# Revit family: KS Husky, Typ II-13, Ø 10- 88,9
name_source: partatom
category: HLS-Bauteile
revit_build: Autodesk Revit 2017 (Build: 20190507_1515(x64)
units: mm (PartAtom-declared; Revit-internal decimal feet)

## family parameters
Arbeitsebenenbasiert = Ja
Beim Laden mit Abzugskörper schneiden = Nein
Bemaßung runder Anschluss = Durchmesser verwenden
Gemeinsam genutzt = Ja
Immer vertikal = Nein
Raumberechnungspunkt = Nein
Teiletyp = Normal

## types (22) — shared parameters
Anschluss = M8/M10
Baustoffklasse = B2
Dichte Kern = 120 kg/m³
Dämmkörper = KA/PU
Fabrikat = MEFA
Firma = MEFA Befestigungs- und Montagesysteme GmbH
H1 = 2 mm  [stored 0.00656168 ft]
HGA = 16 mm  [stored 0.0524934 ft]
Kurztext1 = Kälteschelle Husky II 13
Material = Stahl
Material Mantel = Kunststoff
Materialname = DD11
Mengeneinheit = St
Oberflaeche = galvanisch verzinkt
Rohrschellentyp = Trabant
Typ = II 13
Vorgabe-Ansicht = 1219 mm
Wasserdampfdiffusionswiderstand = 7000 µ
Wärmeleitfähigkeit = 0.029 W/mK
max. Temperaturbeständigkeit = 105 °C
mittl. Nenndruckfestigkeit Kern = 1,35 N/mm²
stat. Belastung Kern = 0,27 N/mm²

## per-type parameters (varying)
- Kälteschelle Husky, Typ II-13, M8/M10, Ø 10: A=30 mm  [stored 0.0984252 ft]; Anschlußhöhe=30 mm; Artikelnummer=6830100; B=75 mm; Breite=69 mm; D=10 mm  [stored 0.0328084 ft]; D0=35 mm  [stored 0.114829 ft]; DF1=19 mm  [stored 0.062336 ft]; DF2=19 mm  [stored 0.062336 ft]; DS=13 mm; DVS=5 mm  [stored 0.0164042 ft]; Dämmstärke=13 mm; EAN=4250928440358; Gewicht=0.06 kg; Gewicht pro Bauteil=0.06 kg; H=53 mm; H2=3 mm  [stored 0.00984252 ft]; Kurztext2=10 mm Iso 13 x 36 mm M8/M10; L=36 mm  [stored 0.11811 ft]; MB=20 mm  [stored 0.0656168 ft]; MD=1 mm  [stored 0.00328084 ft]; R=18 mm  [stored 0.0590551 ft]; RM=19 mm  [stored 0.062336 ft]; Rohraußendurchmesser Kupfer=10 mm; S=56 mm; Schalenlänge=36 mm; max. zul. Last=0.08 kN; vpe=24 St
- Kälteschelle Husky, Typ II-13, M8/M10, Ø 12: A=31 mm  [stored 0.101706 ft]; Anschlußhöhe=31 mm; Artikelnummer=6830120; B=81 mm; Breite=77 mm; D=12 mm  [stored 0.0393701 ft]; D0=39 mm  [stored 0.127953 ft]; DF1=20 mm  [stored 0.0656168 ft]; DF2=20 mm  [stored 0.0656168 ft]; DS=14 mm  [stored 0.0459318 ft]; DVS=5 mm  [stored 0.0164042 ft]; Dämmstärke=14 mm  [stored 0.0459318 ft]; EAN=4250928440365; Gewicht=0.07 kg; Gewicht pro Bauteil=0.07 kg; H=57 mm; H2=3 mm  [stored 0.00984252 ft]; Kurztext2=12 mm Iso 14 x 36 mm M8/M10; L=36 mm  [stored 0.11811 ft]; MB=20 mm  [stored 0.0656168 ft]; MD=1 mm  [stored 0.00328084 ft]; R=20 mm  [stored 0.0656168 ft]; RM=21 mm  [stored 0.0688976 ft]; Rohraußendurchmesser Kunststoff=12 mm; Rohraußendurchmesser Kupfer=12 mm; S=61 mm; Schalenlänge=36 mm; max. zul. Last=0.10 kN; vpe=24 St
- Kälteschelle Husky, Typ II-13, M8/M10, Ø 15: A=30 mm  [stored 0.0984252 ft]; Anschlußhöhe=31 mm; Artikelnummer=6830150; B=81 mm; Breite=77 mm; D=15 mm  [stored 0.0492126 ft]; D0=41 mm  [stored 0.134514 ft]; DF1=19 mm  [stored 0.062336 ft]; DF2=19 mm  [stored 0.062336 ft]; DS=13 mm; DVS=5 mm  [stored 0.0164042 ft]; Dämmstärke=13 mm; EAN=4250928440372; Gewicht=0.07 kg; Gewicht pro Bauteil=0.07 kg; H=59 mm; H2=3 mm  [stored 0.00984252 ft]; Kurztext2=15 mm Iso 13 x 36 mm M8/M10; L=36 mm  [stored 0.11811 ft]; MB=20 mm  [stored 0.0656168 ft]; MD=1 mm  [stored 0.00328084 ft]; R=21 mm  [stored 0.0688976 ft]; RM=22 mm  [stored 0.0721785 ft]; Rohraußendurchmesser Kunststoff=15 mm; Rohraußendurchmesser Kupfer=15 mm; S=62 mm; Schalenlänge=36 mm; max. zul. Last=0.13 kN; vpe=24 St
- Kälteschelle Husky, Typ II-13, M8/M10, Ø 17,2: A=30 mm  [stored 0.0984252 ft]; Anschlußhöhe=31 mm; Artikelnummer=6830180; B=81 mm; Breite=77 mm; D=18 mm  [stored 0.0590551 ft]; D0=44 mm; DF1=17 mm  [stored 0.0557743 ft]; DF2=18 mm  [stored 0.0590551 ft]; DS=13 mm; DVS=5 mm  [stored 0.0164042 ft]; Dämmstärke=13 mm; EAN=4250928440389; Gewicht=0.07 kg; Gewicht pro Bauteil=0.07 kg; H=62 mm; H2=3 mm  [stored 0.00984252 ft]; Kurztext2=17,2 mm Iso 13 x 36 mm M8/M10; L=36 mm  [stored 0.11811 ft]; MB=20 mm  [stored 0.0656168 ft]; MD=1 mm  [stored 0.00328084 ft]; R=22 mm  [stored 0.0721785 ft]; RM=23 mm; Rohraußendurchmesser Kunststoff=18 mm; Rohraußendurchmesser Kupfer=18 mm; Rohraußendurchmesser Stahl=17,2 mm; S=64 mm; Schalenlänge=36 mm; max. zul. Last=0.15 kN; vpe=24 St
- Kälteschelle Husky, Typ II-13, M8/M10, Ø 20: A=32 mm  [stored 0.104987 ft]; Anschlußhöhe=33 mm; Artikelnummer=6830200; B=92 mm; Breite=88 mm; D=20 mm  [stored 0.0656168 ft]; D0=48 mm; DF1=21 mm  [stored 0.0688976 ft]; DF2=20 mm  [stored 0.0656168 ft]; DS=14 mm  [stored 0.0459318 ft]; DVS=5 mm  [stored 0.0164042 ft]; Dämmstärke=14 mm  [stored 0.0459318 ft]; EAN=4250928440396; Gewicht=0.09 kg; Gewicht pro Bauteil=0.09 kg; H=67 mm; H2=3 mm  [stored 0.00984252 ft]; Kurztext2=20 mm Iso 14 x 36 mm M8/M10; L=36 mm  [stored 0.11811 ft]; MB=20 mm  [stored 0.0656168 ft]; MD=2 mm  [stored 0.00656168 ft]; R=24 mm  [stored 0.0787402 ft]; RM=26 mm; Rohraußendurchmesser Kunststoff=20 mm; S=71 mm; Schalenlänge=36 mm; max. zul. Last=0.17 kN; vpe=24 St
- Kälteschelle Husky, Typ II-13, M8/M10, Ø 21,3: A=31 mm  [stored 0.101706 ft]; Anschlußhöhe=32 mm; Artikelnummer=6830220; B=92 mm; Breite=88 mm; D=22 mm  [stored 0.0721785 ft]; D0=48 mm; DF1=21 mm  [stored 0.0688976 ft]; DF2=20 mm  [stored 0.0656168 ft]; DS=13 mm; DVS=5 mm  [stored 0.0164042 ft]; Dämmstärke=13 mm; EAN=4250928440402; Gewicht=0.09 kg; Gewicht pro Bauteil=0.09 kg; H=67 mm; H2=3 mm  [stored 0.00984252 ft]; Kurztext2=21,3 mm Iso 13 x 36 mm M8/M10; L=36 mm  [stored 0.11811 ft]; MB=20 mm  [stored 0.0656168 ft]; MD=2 mm  [stored 0.00656168 ft]; R=24 mm  [stored 0.0787402 ft]; RM=26 mm; Rohraußendurchmesser Kupfer=22 mm; Rohraußendurchmesser Stahl=21,3 mm; S=71 mm; Schalenlänge=36 mm; max. zul. Last=0.19 kN; vpe=24 St
- Kälteschelle Husky, Typ II-13, M8/M10, Ø 26,9: A=31 mm  [stored 0.101706 ft]; Anschlußhöhe=32 mm; Artikelnummer=6830270; B=92 mm; Breite=88 mm; D=27 mm; D0=53 mm; DF1=18 mm  [stored 0.0590551 ft]; DF2=18 mm  [stored 0.0590551 ft]; DS=13 mm; DVS=5 mm  [stored 0.0164042 ft]; Dämmstärke=13 mm; EAN=4250928440426; Gewicht=0.09 kg; Gewicht pro Bauteil=0.09 kg; H=72 mm; H2=3 mm  [stored 0.00984252 ft]; Kurztext2=26,9 mm Iso 13 x 36 mm M8/M10; L=36 mm  [stored 0.11811 ft]; MB=20 mm  [stored 0.0656168 ft]; MD=2 mm  [stored 0.00656168 ft]; R=27 mm; RM=28 mm  [stored 0.0918635 ft]; Rohraußendurchmesser Stahl=26,9 mm; S=74 mm; Schalenlänge=36 mm; max. zul. Last=0.23 kN; vpe=12 St
- Kälteschelle Husky, Typ II-13, M8/M10, Ø 28: A=30 mm  [stored 0.0984252 ft]; Anschlußhöhe=32 mm; Artikelnummer=6830280; B=92 mm; Breite=88 mm; D=28 mm  [stored 0.0918635 ft]; D0=53 mm; DF1=18 mm  [stored 0.0590551 ft]; DF2=18 mm  [stored 0.0590551 ft]; DS=13 mm; DVS=5 mm  [stored 0.0164042 ft]; Dämmstärke=13 mm; EAN=4250928440433; Gewicht=0.09 kg; Gewicht pro Bauteil=0.09 kg; H=72 mm; H2=3 mm  [stored 0.00984252 ft]; Kurztext2=28 mm Iso 13 x 36 mm M8/M10; L=36 mm  [stored 0.11811 ft]; MB=20 mm  [stored 0.0656168 ft]; MD=2 mm  [stored 0.00656168 ft]; R=27 mm; RM=28 mm  [stored 0.0918635 ft]; Rohraußendurchmesser Kupfer=28 mm; S=74 mm; Schalenlänge=36 mm; max. zul. Last=0.24 kN; vpe=12 St
- Kälteschelle Husky, Typ II-13, M8/M10, Ø 31,8: A=31 mm  [stored 0.101706 ft]; Anschlußhöhe=32 mm; Artikelnummer=6830320; B=98 mm; Breite=94 mm; D=32 mm  [stored 0.104987 ft]; D0=58 mm; DF1=19 mm  [stored 0.062336 ft]; DF2=18 mm  [stored 0.0590551 ft]; DS=13 mm; DVS=5 mm  [stored 0.0164042 ft]; Dämmstärke=13 mm; EAN=4250928440440; Gewicht=0.10 kg; Gewicht pro Bauteil=0.10 kg; H=77 mm; H2=3 mm  [stored 0.00984252 ft]; Kurztext2=31,8 mm Iso 13 x 36 mm M8/M10; L=36 mm  [stored 0.11811 ft]; MB=20 mm  [stored 0.0656168 ft]; MD=2 mm  [stored 0.00656168 ft]; R=29 mm  [stored 0.0951444 ft]; RM=31 mm  [stored 0.101706 ft]; Rohraußendurchmesser Kunststoff=32 mm; Rohraußendurchmesser Stahl=31,8 mm; S=79 mm; Schalenlänge=36 mm; max. zul. Last=0.27 kN; vpe=12 St
- Kälteschelle Husky, Typ II-13, M8/M10, Ø 33,7: A=32 mm  [stored 0.104987 ft]; Anschlußhöhe=33 mm; Artikelnummer=6830340; B=104 mm; Breite=102 mm; D=34 mm; D0=62 mm; DF1=20 mm  [stored 0.0656168 ft]; DF2=19 mm  [stored 0.062336 ft]; DS=14 mm  [stored 0.0459318 ft]; DVS=5 mm  [stored 0.0164042 ft]; Dämmstärke=14 mm  [stored 0.0459318 ft]; EAN=4250928440457; Gewicht=0.11 kg; Gewicht pro Bauteil=0.11 kg; H=81 mm; H2=3 mm  [stored 0.00984252 ft]; Kurztext2=33,7 mm Iso 14 x 36 mm M8/M10; L=36 mm  [stored 0.11811 ft]; MB=20 mm  [stored 0.0656168 ft]; MD=2 mm  [stored 0.00656168 ft]; R=31 mm  [stored 0.101706 ft]; RM=33 mm  [stored 0.108268 ft]; Rohraußendurchmesser Stahl=33,7 mm; S=84 mm; Schalenlänge=36 mm; max. zul. Last=0.29 kN; vpe=12 St
- Kälteschelle Husky, Typ II-13, M8/M10, Ø 35: A=31 mm  [stored 0.101706 ft]; Anschlußhöhe=32 mm; Artikelnummer=6830350; B=104 mm; Breite=102 mm; D=35 mm  [stored 0.114829 ft]; D0=62 mm; DF1=20 mm  [stored 0.0656168 ft]; DF2=19 mm  [stored 0.062336 ft]; DS=14 mm  [stored 0.0459318 ft]; DVS=5 mm  [stored 0.0164042 ft]; Dämmstärke=14 mm  [stored 0.0459318 ft]; EAN=4250928440464; Gewicht=0.10 kg; Gewicht pro Bauteil=0.10 kg; H=81 mm; H2=3 mm  [stored 0.00984252 ft]; Kurztext2=35 mm Iso 14 x 36 mm M8/M10; L=36 mm  [stored 0.11811 ft]; MB=20 mm  [stored 0.0656168 ft]; MD=2 mm  [stored 0.00656168 ft]; R=31 mm  [stored 0.101706 ft]; RM=33 mm  [stored 0.108268 ft]; Rohraußendurchmesser Kupfer=35 mm; S=84 mm; Schalenlänge=36 mm; max. zul. Last=0.30 kN; vpe=12 St
- Kälteschelle Husky, Typ II-13, M8/M10, Ø 40: A=32 mm  [stored 0.104987 ft]; Anschlußhöhe=33 mm; Artikelnummer=6830400; B=111 mm; Breite=109 mm; D=40 mm  [stored 0.131234 ft]; D0=68 mm; DF1=20 mm  [stored 0.0656168 ft]; DF2=20 mm  [stored 0.0656168 ft]; DS=14 mm  [stored 0.0459318 ft]; DVS=5 mm  [stored 0.0164042 ft]; Dämmstärke=14 mm  [stored 0.0459318 ft]; EAN=4250928440471; Gewicht=0.11 kg; Gewicht pro Bauteil=0.11 kg; H=87 mm; H2=3 mm  [stored 0.00984252 ft]; Kurztext2=40 mm Iso 14 x 36 mm M8/M10; L=36 mm  [stored 0.11811 ft]; MB=20 mm  [stored 0.0656168 ft]; MD=2 mm  [stored 0.00656168 ft]; R=34 mm; RM=36 mm  [stored 0.11811 ft]; Rohraußendurchmesser Kunststoff=40 mm; S=91 mm; Schalenlänge=36 mm; max. zul. Last=0.34 kN; vpe=12 St
- Kälteschelle Husky, Typ II-13, M8/M10, Ø 42,4: A=31 mm  [stored 0.101706 ft]; Anschlußhöhe=32 mm; Artikelnummer=6830420; B=111 mm; Breite=109 mm; D=42 mm  [stored 0.137795 ft]; D0=70 mm; DF1=19 mm  [stored 0.062336 ft]; DF2=19 mm  [stored 0.062336 ft]; DS=14 mm  [stored 0.0459318 ft]; DVS=5 mm  [stored 0.0164042 ft]; Dämmstärke=14 mm  [stored 0.0459318 ft]; EAN=4250928440488; Gewicht=0.11 kg; Gewicht pro Bauteil=0.11 kg; H=89 mm; H2=3 mm  [stored 0.00984252 ft]; Kurztext2=42,4 mm Iso 14 x 36 mm M8/M10; L=36 mm  [stored 0.11811 ft]; MB=20 mm  [stored 0.0656168 ft]; MD=2 mm  [stored 0.00656168 ft]; R=35 mm  [stored 0.114829 ft]; RM=37 mm; Rohraußendurchmesser Kupfer=42 mm; Rohraußendurchmesser Stahl=42,4 mm; S=92 mm; Schalenlänge=36 mm; max. zul. Last=0.36 kN; vpe=12 St
- Kälteschelle Husky, Typ II-13, M8/M10, Ø 48,3: A=32 mm  [stored 0.104987 ft]; Anschlußhöhe=33 mm; Artikelnummer=6830480; B=122 mm; Breite=121 mm; D=48 mm; D0=78 mm; DF1=21 mm  [stored 0.0688976 ft]; DF2=20 mm  [stored 0.0656168 ft]; DS=15 mm  [stored 0.0492126 ft]; DVS=5 mm  [stored 0.0164042 ft]; Dämmstärke=15 mm  [stored 0.0492126 ft]; EAN=4250928440495; Gewicht=0.14 kg; Gewicht pro Bauteil=0.14 kg; H=97 mm; H2=3 mm  [stored 0.00984252 ft]; Kurztext2=48,3 mm Iso 15 x 42 mm M8/M10; L=42 mm  [stored 0.137795 ft]; MB=25 mm  [stored 0.082021 ft]; MD=2 mm  [stored 0.00656168 ft]; R=39 mm  [stored 0.127953 ft]; RM=41 mm  [stored 0.134514 ft]; Rohraußendurchmesser Stahl=48,3 mm; S=101 mm; Schalenlänge=42 mm; max. zul. Last=0.48 kN; vpe=10 St
- Kälteschelle Husky, Typ II-13, M8/M10, Ø 50: A=32 mm  [stored 0.104987 ft]; Anschlußhöhe=33 mm; Artikelnummer=6830500; B=122 mm; Breite=121 mm; D=50 mm; D0=79 mm; DF1=20 mm  [stored 0.0656168 ft]; DF2=20 mm  [stored 0.0656168 ft]; DS=15 mm  [stored 0.0492126 ft]; DVS=5 mm  [stored 0.0164042 ft]; Dämmstärke=15 mm  [stored 0.0492126 ft]; EAN=4250928440501; Gewicht=0.14 kg; Gewicht pro Bauteil=0.14 kg; H=98 mm; H2=3 mm  [stored 0.00984252 ft]; Kurztext2=50 mm Iso 15 x 42 mm M8/M10; L=42 mm  [stored 0.137795 ft]; MB=25 mm  [stored 0.082021 ft]; MD=2 mm  [stored 0.00656168 ft]; R=40 mm  [stored 0.131234 ft]; RM=41 mm  [stored 0.134514 ft]; Rohraußendurchmesser Kunststoff=50 mm; S=102 mm; Schalenlänge=42 mm; max. zul. Last=0.49 kN; vpe=10 St
- Kälteschelle Husky, Typ II-13, M8/M10, Ø 54: A=32 mm  [stored 0.104987 ft]; Anschlußhöhe=33 mm; Artikelnummer=6830540; B=127 mm; Breite=124 mm; D=54 mm; D0=83 mm; DF1=21 mm  [stored 0.0688976 ft]; DF2=20 mm  [stored 0.0656168 ft]; DS=15 mm  [stored 0.0492126 ft]; DVS=5 mm  [stored 0.0164042 ft]; Dämmstärke=15 mm  [stored 0.0492126 ft]; EAN=4250928440518; Gewicht=0.15 kg; Gewicht pro Bauteil=0.15 kg; H=102 mm; H2=3 mm  [stored 0.00984252 ft]; Kurztext2=54 mm Iso 15 x 42 mm M8/M10; L=42 mm  [stored 0.137795 ft]; MB=25 mm  [stored 0.082021 ft]; MD=2 mm  [stored 0.00656168 ft]; R=42 mm  [stored 0.137795 ft]; RM=43 mm  [stored 0.141076 ft]; Rohraußendurchmesser Kupfer=54 mm; S=106 mm; Schalenlänge=42 mm; max. zul. Last=0.53 kN; vpe=10 St
- Kälteschelle Husky, Typ II-13, M8/M10, Ø 57: A=32 mm  [stored 0.104987 ft]; Anschlußhöhe=33 mm; Artikelnummer=6830570; B=127 mm; Breite=124 mm; D=57 mm; D0=86 mm; DF1=19 mm  [stored 0.062336 ft]; DF2=19 mm  [stored 0.062336 ft]; DS=15 mm  [stored 0.0492126 ft]; DVS=5 mm  [stored 0.0164042 ft]; Dämmstärke=15 mm  [stored 0.0492126 ft]; EAN=4250928440525; Gewicht=0.15 kg; Gewicht pro Bauteil=0.15 kg; H=105 mm; H2=3 mm  [stored 0.00984252 ft]; Kurztext2=57 mm Iso 15 x 42 mm M8/M10; L=42 mm  [stored 0.137795 ft]; MB=25 mm  [stored 0.082021 ft]; MD=2 mm  [stored 0.00656168 ft]; R=43 mm  [stored 0.141076 ft]; RM=45 mm; Rohraußendurchmesser Stahl=57 mm; S=108 mm; Schalenlänge=42 mm; max. zul. Last=0.56 kN; vpe=10 St
- Kälteschelle Husky, Typ II-13, M8/M10, Ø 60,3: A=35 mm  [stored 0.114829 ft]; Anschlußhöhe=35 mm; Artikelnummer=6830600; B=134 mm; Breite=134 mm; D=60 mm; D0=94 mm; DF1=18 mm  [stored 0.0590551 ft]; DF2=18 mm  [stored 0.0590551 ft]; DS=17 mm  [stored 0.0557743 ft]; DVS=5 mm  [stored 0.0164042 ft]; Dämmstärke=17 mm  [stored 0.0557743 ft]; EAN=4250928440532; Gewicht=0.20 kg; Gewicht pro Bauteil=0.20 kg; H=114 mm; H2=4 mm  [stored 0.0131234 ft]; Kurztext2=60,3 mm Iso 17 x 42 mm M8/M10; L=42 mm  [stored 0.137795 ft]; MB=25 mm  [stored 0.082021 ft]; MD=2 mm  [stored 0.00656168 ft]; R=47 mm; RM=49 mm; Rohraußendurchmesser Stahl=60,3 mm; S=116 mm; Schalenlänge=42 mm; max. zul. Last=0.60 kN; vpe=10 St
- Kälteschelle Husky, Typ II-13, M8/M10, Ø 63,5: A=33 mm  [stored 0.108268 ft]; Anschlußhöhe=34 mm; Artikelnummer=6830640; B=134 mm; Breite=134 mm; D=64 mm; D0=94 mm; DF1=18 mm  [stored 0.0590551 ft]; DF2=18 mm  [stored 0.0590551 ft]; DS=15 mm  [stored 0.0492126 ft]; DVS=6 mm  [stored 0.019685 ft]; Dämmstärke=15 mm  [stored 0.0492126 ft]; EAN=4250928440549; Gewicht=0.20 kg; Gewicht pro Bauteil=0.20 kg; H=114 mm; H2=4 mm  [stored 0.0131234 ft]; Kurztext2=63,5 mm Iso 15 x 42 mm M8/M10; L=42 mm  [stored 0.137795 ft]; MB=25 mm  [stored 0.082021 ft]; MD=2 mm  [stored 0.00656168 ft]; R=47 mm; RM=49 mm; Rohraußendurchmesser Kupfer=64 mm; Rohraußendurchmesser Stahl=63,5 mm; S=116 mm; Schalenlänge=42 mm; max. zul. Last=0.63 kN; vpe=10 St
- Kälteschelle Husky, Typ II-13, M8/M10, Ø 70: A=32 mm  [stored 0.104987 ft]; Anschlußhöhe=32 mm; Artikelnummer=6830700; B=134 mm; Breite=134 mm; D=70 mm; D0=97 mm; DF1=17 mm  [stored 0.0557743 ft]; DF2=16 mm  [stored 0.0524934 ft]; DS=14 mm  [stored 0.0459318 ft]; DVS=6 mm  [stored 0.019685 ft]; Dämmstärke=14 mm  [stored 0.0459318 ft]; EAN=4250928440556; Gewicht=0.20 kg; Gewicht pro Bauteil=0.20 kg; H=117 mm; H2=4 mm  [stored 0.0131234 ft]; Kurztext2=70 mm Iso 14 x 42 mm M8/M10; L=42 mm  [stored 0.137795 ft]; MB=25 mm  [stored 0.082021 ft]; MD=2 mm  [stored 0.00656168 ft]; R=49 mm; RM=51 mm; Rohraußendurchmesser Stahl=70 mm; S=117 mm; Schalenlänge=42 mm; max. zul. Last=0.69 kN; vpe=8 St
- Kälteschelle Husky, Typ II-13, M8/M10, Ø 76,1: A=35 mm  [stored 0.114829 ft]; Anschlußhöhe=34 mm; Artikelnummer=6830761; B=153 mm; Breite=153 mm; D=76 mm; D0=108 mm; DF1=20 mm  [stored 0.0656168 ft]; DF2=20 mm  [stored 0.0656168 ft]; DS=16 mm  [stored 0.0524934 ft]; DVS=6 mm  [stored 0.019685 ft]; Dämmstärke=16 mm  [stored 0.0524934 ft]; EAN=4250928440563; Gewicht=0.27 kg; Gewicht pro Bauteil=0.27 kg; H=129 mm; H2=4 mm  [stored 0.0131234 ft]; Kurztext2=76,1 mm Iso 16 x 42 mm M8/M10; L=42 mm  [stored 0.137795 ft]; MB=25 mm  [stored 0.082021 ft]; MD=3 mm  [stored 0.00984252 ft]; R=54 mm; RM=57 mm; Rohraußendurchmesser Stahl=76,1 mm; S=133 mm; Schalenlänge=42 mm; max. zul. Last=0.75 kN; vpe=8 St
- Kälteschelle Husky, Typ II-13, M8/M10, Ø 88,9: A=35 mm  [stored 0.114829 ft]; Anschlußhöhe=35 mm; Artikelnummer=6830891; B=166 mm; Breite=165 mm; D=89 mm; D0=121 mm; DF1=20 mm  [stored 0.0656168 ft]; DF2=20 mm  [stored 0.0656168 ft]; DS=16 mm  [stored 0.0524934 ft]; DVS=6 mm  [stored 0.019685 ft]; Dämmstärke=16 mm  [stored 0.0524934 ft]; EAN=4250928440570; Gewicht=0.28 kg; Gewicht pro Bauteil=0.28 kg; H=142 mm; H2=4 mm  [stored 0.0131234 ft]; Kurztext2=88,9 mm Iso 16 x 42 mm M8/M10; L=42 mm  [stored 0.137795 ft]; MB=25 mm  [stored 0.082021 ft]; MD=3 mm  [stored 0.00984252 ft]; R=61 mm; RM=63 mm; Rohraußendurchmesser Stahl=88,9 mm; S=146 mm; Schalenlänge=42 mm; max. zul. Last=0.86 kN; vpe=8 St

note: [stored X ft] marks values corroborated as IEEE doubles in the binary element streams (Revit-internal decimal feet)

## geometry (parser evidence)
native form markers: Sweep x3
no freeform markers — native parametric forms only
